# Revit family: Porta VV dupla
name_source: partatom
category: Doors
units: mm (PartAtom-declared; Revit-internal decimal feet)

## family parameters
Cut with Voids When Loaded = Yes
Host = Face
OmniClass Number = 23.30.10.00
OmniClass Title = Doors
Room Calculation Point = No
Shared = No

## types (1)
- 50 - 1000 x 2100
    Altura Vao Luz = 2200 mm
    Analytic Construction = Metal, fiberglass core
    Bumper asa de aviao = Yes
    Chapa xadrez = No
    Default Elevation = 0 mm  [stored 0 ft]
    Define Thermal Properties by = Schematic Type
    Espessura Folha = 40 mm  [stored 0.131234 ft]
    Function = Interior
    Heat Transfer Coefficient (U) = 3.35 W/(m²·K)
    Height = 2200 mm
    Largura Vao Luz = 1800 mm  [stored 5.90551 ft]
    Largura folha = 893 mm  [stored 2.92979 ft]
    Operation = Double Swing
    Solar Heat Gain Coefficient = 0
    Thermal Resistance (R) = 0.2985 (m²·K)/W
    Visual Light Transmittance = 0
    Width = 1800 mm  [stored 5.90551 ft]

note: [stored X ft] marks values corroborated as IEEE doubles in the binary element streams (Revit-internal decimal feet)

## geometry (parser evidence)
native form markers: Blend x2
no freeform markers — native parametric forms only
